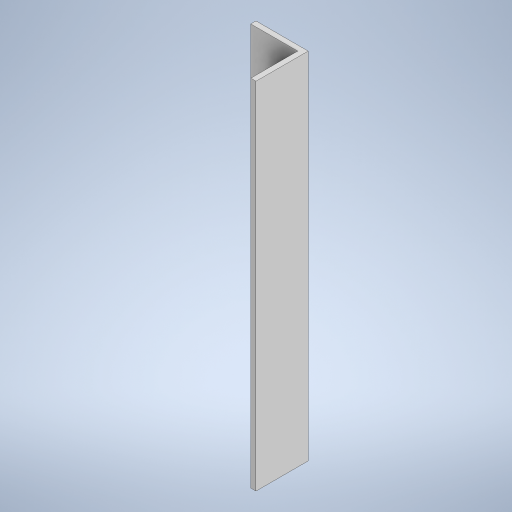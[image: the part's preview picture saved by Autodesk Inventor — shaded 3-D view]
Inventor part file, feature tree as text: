
AUTODESK INVENTOR PART (.ipt)
format: ipt  version: 2024 (Build 280153000, 153)  size: 231,936 bytes
history: native  units: mm
features: extrude x1, sketch x1
ambient origin geometry x8: Origin, YZ Plane, XZ Plane, XY Plane, X Axis, Y Axis, Z Axis, Center Point
bodies: Solid1 (feature_tree)
feature tree (2):
  extrude  "Extrusion1"  Depth=50.0mm
  sketch  "Sketch1"  dims[d0=50.0mm d1=50.0mm d2=5.0mm d3=340.0mm d4=0.0mm]
